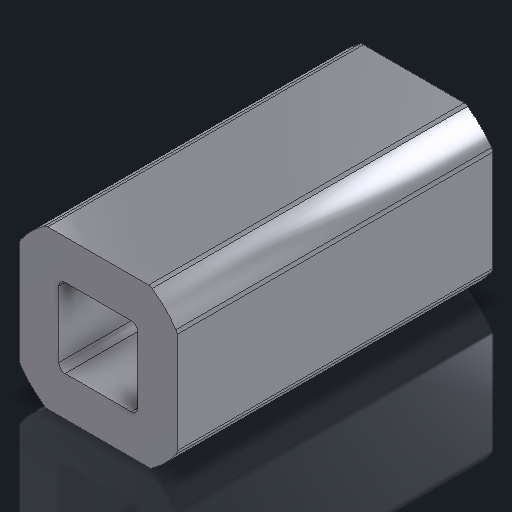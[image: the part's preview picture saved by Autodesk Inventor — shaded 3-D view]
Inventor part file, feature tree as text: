
AUTODESK INVENTOR PART (.ipt)
format: ipt  version: 2023.2 (Build 272271030, 271C)  size: 174,080 bytes
history: native  units: in
note: dims shown in document units (in); Inventor stores cm internally (conversion verified against a paired STEP export)
features: other x3, sketch x2
ambient origin geometry x8: Origin, YZ Plane, XZ Plane, XY Plane, X Axis, Y Axis, Z Axis, Center Point
bodies: Solid1 (feature_tree)
feature tree (5):
  other  "HS Shaft Adapter Square.ipt"
  other  "Solid1::HS Shaft Adapter Square.ipt"
  other  "TaggingFeature1"
  sketch  "Sketch1"  dims[d0=0.3937in]
  sketch  "Sketch2"
